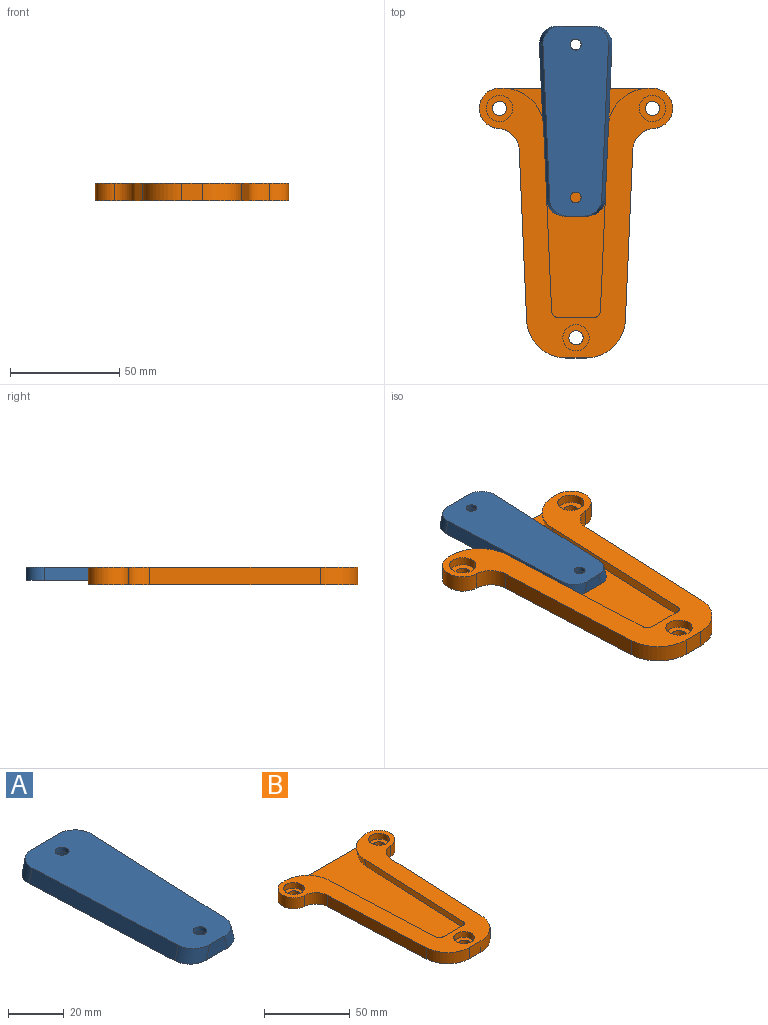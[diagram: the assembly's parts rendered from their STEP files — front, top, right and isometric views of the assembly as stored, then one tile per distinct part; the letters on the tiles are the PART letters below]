
ASSEMBLY  parts=2 mates=1
PART A: 16 faces, bbox 33.2x87x10.1 mm
  f0: cylinder r=2.5mm len=5mm, axis (0,0,1), area 31.4mm2, adj f3,f14
  f1: cylinder r=2.5mm len=5mm, axis (0,0,1), area 31.4mm2, adj f3,f12
  f2: plane 71x6mm, normal (0.97,-0.04,0.26), area 441.4mm2, adj f3,f4,f7,f8
  f3: plane 87x30.03mm, normal (0,0,1), area 2247.7mm2, adj f0,f1,f2,f5,f6,f7,f8,f9
  f4: plane 87x33.25mm, normal (0,0,-1), area 2409.9mm2, adj f2,f5,f6,f7,f8,f9,f10,f11
  f5: plane 16.68x6mm, normal (0,1,0), area 90.4mm2, adj f3,f4,f7,f10
  f6: plane 10.48x6mm, normal (0,-1,0), area 53.2mm2, adj f3,f4,f8,f11
  f7: cylinder r=8mm len=10.15mm, axis (0.26,0,-0.97), area 80.2mm2, adj f2,f3,f4,f5
  f8: cylinder r=8mm len=10.14mm, axis (-0.26,0,0.97), area 76mm2, adj f2,f3,f4,f6
  f9: plane 71x6mm, normal (-0.97,-0.04,0.26), area 441.4mm2, adj f3,f4,f10,f11
  f10: cylinder r=8mm len=10.15mm, axis (-0.26,0,-0.97), area 80.2mm2, adj f3,f4,f5,f9
  f11: cylinder r=8mm len=10.14mm, axis (0.26,0,0.97), area 76mm2, adj f3,f4,f6,f9
  f12: plane 10x10mm, normal (0,0,-1), area 58.9mm2, adj f1,f13
  f13: cylinder r=5mm len=10mm, axis (0,0,-1), area 125.7mm2, adj f4,f12
  f14: plane 10x10mm, normal (0,0,-1), area 58.9mm2, adj f0,f15
  f15: cylinder r=5mm len=10mm, axis (0,0,-1), area 125.7mm2, adj f4,f14
PART B: 31 faces, bbox 88.5x123.5x15.3 mm
  f0: cylinder r=3.25mm len=6.5mm, axis (0,0,1), area 81.7mm2, adj f8,f19
  f1: cylinder r=3.25mm len=6.5mm, axis (0,0,1), area 81.7mm2, adj f8,f16
  f2: plane 70x2mm, normal (0,1,0), area 140mm2, adj f7,f8,f11,f23
  f3: plane 5.63x1.51mm, normal (0,1,0), area 4.3mm2, adj f4,f7,f14
  f4: plane 123.5x88.5mm, normal (0,0,1), area 3280.8mm2, adj f3,f5,f6,f7,f9,f10,f12,f13
  f5: plane 9.24x8mm, normal (0,-1,0), area 73.9mm2, adj f4,f8,f15,f28
  f6: plane 78.25x8mm, normal (1,-0.04,0), area 626.6mm2, adj f4,f8,f9,f15
  f7: cylinder r=9.25mm len=18.49mm, axis (0,0,1), area 228.6mm2, adj f2,f3,f4,f8,f9,f11,f14
  f8: plane 123.5x88.5mm, normal (0,0,-1), area 6446.6mm2, adj f0,f1,f2,f5,f6,f7,f9,f15
  f9: cylinder r=10mm len=9.55mm, axis (0,0,1), area 118mm2, adj f4,f6,f7,f8
  f10: plane 84.88x6mm, normal (-0.97,0.04,-0.26), area 527.8mm2, adj f4,f11,f13,f14
  f11: plane 105x70.08mm, normal (0,0,1), area 3264mm2, adj f2,f7,f10,f12,f13,f14,f23,f25
  f12: plane 19.34x6mm, normal (0,1,0), area 106.4mm2, adj f4,f11,f13,f26
  f13: cylinder r=3mm len=7.55mm, axis (0.26,0,-0.97), area 28.5mm2, adj f4,f10,f11,f12
  f14: cylinder r=18mm len=20.23mm, axis (0.26,0,-0.97), area 170.9mm2, adj f3,f4,f7,f10,f11
  f15: cylinder r=18mm len=17.98mm, axis (0,0,1), area 219.9mm2, adj f4,f5,f6,f8
  f16: plane 12x12mm, normal (0,0,1), area 79.9mm2, adj f1,f17
  f17: cylinder r=6mm len=12mm, axis (0,0,1), area 150.8mm2, adj f4,f16
  f18: cylinder r=6mm len=12mm, axis (0,0,1), area 150.8mm2, adj f4,f19
  f19: plane 12x12mm, normal (0,0,1), area 79.9mm2, adj f0,f18
  f20: cylinder r=3.25mm len=6.5mm, axis (0,0,1), area 81.7mm2, adj f8,f29
  f21: plane 5.63x1.51mm, normal (0,1,0), area 4.3mm2, adj f4,f23,f27
  f22: plane 78.25x8mm, normal (-1,-0.04,0), area 626.6mm2, adj f4,f8,f24,f28
  f23: cylinder r=9.25mm len=18.49mm, axis (0,0,1), area 228.6mm2, adj f2,f4,f8,f11,f21,f24,f27
  f24: cylinder r=10mm len=9.55mm, axis (0,0,1), area 118mm2, adj f4,f8,f22,f23
  f25: plane 84.88x6mm, normal (0.97,0.04,-0.26), area 527.8mm2, adj f4,f11,f26,f27
  f26: cylinder r=3mm len=7.55mm, axis (-0.26,0,-0.97), area 28.5mm2, adj f4,f11,f12,f25
  f27: cylinder r=18mm len=20.23mm, axis (-0.26,0,-0.97), area 170.9mm2, adj f4,f11,f21,f23,f25
  f28: cylinder r=18mm len=17.98mm, axis (0,0,1), area 219.9mm2, adj f4,f5,f8,f22
  f29: plane 12x12mm, normal (0,0,1), area 79.9mm2, adj f20,f30
  f30: cylinder r=6mm len=12mm, axis (0,0,1), area 150.8mm2, adj f4,f29
PLACE A t=(7.86,51.81,15.07)mm
PLACE B t=(8,17.59,15.07)mm fixed
MATE planar A.f4 <-> B.f11  axis (0,0,-1) through (7.86,53.7,9.07)mm
